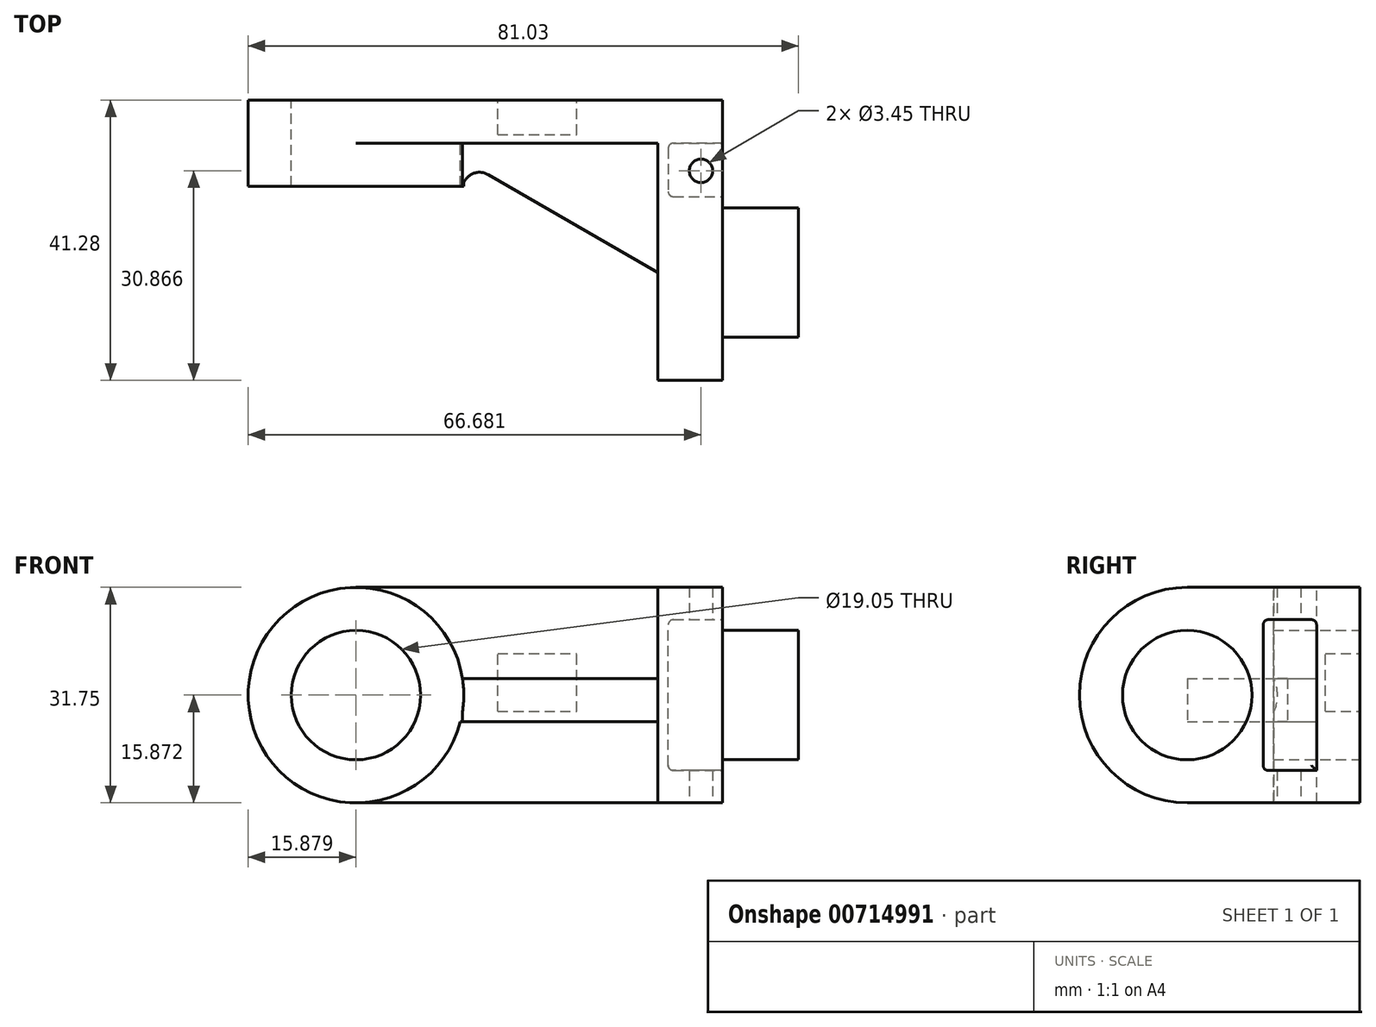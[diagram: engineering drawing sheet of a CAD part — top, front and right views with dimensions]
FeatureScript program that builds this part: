
annotation { "Feature Type Name" : "Feature", "Feature Type Description" : "" }
export const myFeature = defineFeature(function(context is Context, id is Id, definition is map)
    precondition{}
    {
        {
            var Q0;
            Q0=qCreatedBy(makeId("Front.planeOp"),FACE);
            var sketch = newSketch(context, id + "F0", { "sketchPlane" : qUnion([Q0])});
            skLineSegment(sketch, "E0", {"start": v(12.77, -13.47) * mm, "end": v(-41.2, -13.47) * mm});
            skLineSegment(sketch, "E1", {"start": v(12.77, -13.47) * mm, "end": v(12.77, 18.28) * mm});
            skLineSegment(sketch, "E2", {"start": v(12.77, 18.28) * mm, "end": v(-41.2, 18.28) * mm});
            skCircle(sketch, "E3", {"center": v(-41.2, 2.4) * mm, "radius": 15.88 * mm});
            skPoint(sketch, "E3.third.point", {"position": v(-56.86, -0.22) * mm});
            skCircle(sketch, "E4", {"center": v(-41.2, 2.4) * mm, "radius": 9.53 * mm});
            skSolve(sketch);
        }
        {
            var Q0;
            Q0 = qSketchRegion(id + "F0", true);
            extrude(context, id + "F1", {"entities" : qUnion([Q0]), "depth" : 6.35 * mm, "offsetDistance" : 25.4 * mm});
        }
        {
            var Q0;
            Q0=makeQuery(id+"F1.opExtrude","CAP_FACE",FACE,{"disambiguationData":[OSD([sQuery(id+"F0.wireOp",EDGE,"E0"),sQuery(id+"F0.wireOp",EDGE,"E1"),sQuery(id+"F0.wireOp",EDGE,"E2"),sQuery(id+"F0.wireOp",EDGE,"E3"),sQuery(id+"F0.wireOp",EDGE,"E4")])],"isStart":false});
            var sketch = newSketch(context, id + "F2", { "sketchPlane" : qUnion([Q0])});
            skCircle(sketch, "E5", {"center": v(-41.2, 2.4) * mm, "radius": 9.53 * mm});
            skCircle(sketch, "E6", {"center": v(-41.2, 2.4) * mm, "radius": 15.88 * mm});
            skSolve(sketch);
        }
        {
            var Q0;
            Q0 = qSketchRegion(id + "F2", true);
            extrude(context, id + "F3", {"entities" : qUnion([Q0]), "operationType" : NewBodyOperationType.ADD, "depth" : 6.35 * mm, "offsetDistance" : 25.4 * mm});
        }
        {
            var Q0;
            Q0=qCreatedBy(makeId("Right.planeOp"),FACE);
            cPlane(context, id + "F4", {"entities" : qUnion([Q0]), "cplaneType" : CPlaneType.OFFSET, "offset" : 12.78 * mm, "width" : 152.4 * mm, "height" : 152.4 * mm});
        }
        {
            var Q0;
            Q0=qCreatedBy(id+"F4.planeOp",FACE);
            var sketch = newSketch(context, id + "F5", { "sketchPlane" : qUnion([Q0])});
            skLineSegment(sketch, "E7", {"start": v(-6.35, -13.47) * mm, "end": v(-25.4, -13.47) * mm});
            skLineSegment(sketch, "E8", {"start": v(-6.35, 18.28) * mm, "end": v(-25.4, 18.28) * mm});
            skArc(sketch, "E9", {"start": v(-25.4, 18.28) * mm, "mid": v(-41.28, 2.4) * mm, "end": v(-25.4, -13.47) * mm});
            skLineSegment(sketch, "E10", {"start": v(-6.35, -13.47) * mm, "end": v(-6.35, 18.28) * mm});
            skSolve(sketch);
        }
        {
            var Q0;
            Q0 = qSketchRegion(id + "F5", true);
            extrude(context, id + "F6", {"entities" : qUnion([Q0]), "operationType" : NewBodyOperationType.ADD, "oppositeDirection" : true, "depth" : 9.52 * mm, "offsetDistance" : 25.4 * mm});
        }
        {
            var Q0;
            Q0=makeQuery(id+"F6.opExtrude","CAP_FACE",FACE,{"disambiguationData":[OSD([sQuery(id+"F5.wireOp",EDGE,"E7"),sQuery(id+"F5.wireOp",EDGE,"E8"),sQuery(id+"F5.wireOp",EDGE,"E9"),sQuery(id+"F5.wireOp",EDGE,"E10")])],"isStart":true});
            var sketch = newSketch(context, id + "F7", { "sketchPlane" : qUnion([Q0])});
            skCircle(sketch, "E11", {"center": v(-25.4, 2.4) * mm, "radius": 9.52 * mm});
            skSolve(sketch);
        }
        {
            var Q0;
            Q0 = qSketchRegion(id + "F7", true);
            extrude(context, id + "F8", {"entities" : qUnion([Q0]), "operationType" : NewBodyOperationType.ADD, "depth" : 11.18 * mm, "offsetDistance" : 25.4 * mm});
        }
        {
            var Q0;
            Q0=qCreatedBy(makeId("Top.planeOp"),FACE);
            var sketch = newSketch(context, id + "F9", { "sketchPlane" : qUnion([Q0])});
            skLineSegment(sketch, "E12", {"start": v(3.25, -25.4) * mm, "end": v(-21.74, -10.97) * mm});
            skLineSegment(sketch, "E13", {"start": v(3.25, -25.4) * mm, "end": v(3.25, -6.35) * mm});
            skLineSegment(sketch, "E14", {"start": v(3.25, -6.35) * mm, "end": v(-25.51, -6.35) * mm});
            skArc(sketch, "E15", {"start": v(-21.74, -10.97) * mm, "mid": v(-24.08, -10.86) * mm, "end": v(-25.51, -12.7) * mm});
            skLineSegment(sketch, "E16", {"start": v(-25.51, -12.7) * mm, "end": v(-28.97, -12.7) * mm});
            skLineSegment(sketch, "E17", {"start": v(-28.97, -6.38) * mm, "end": v(-25.51, -6.35) * mm});
            skLineSegment(sketch, "E18", {"start": v(-28.97, -6.38) * mm, "end": v(-28.97, -12.7) * mm});
            skLineSegment(sketch, "E19", {"start": v(-25.51, -12.7) * mm, "end": v(-25.51, -6.35) * mm});
            skSolve(sketch);
        }
        {
            var Q0;
            Q0 = qSketchRegion(id + "F9", true);
            extrude(context, id + "F10", {"entities" : qUnion([Q0]), "operationType" : NewBodyOperationType.ADD, "depth" : 4.83 * mm, "offsetDistance" : 25.4 * mm, "hasSecondDirection" : true, "secondDirectionOppositeDirection" : true, "secondDirectionDepth" : 1.52 * mm});
        }
        {
            var Q0;
            Q0=makeQuery(id+"F6.opExtrude","CAP_FACE",FACE,{"disambiguationData":[OSD([sQuery(id+"F5.wireOp",EDGE,"E7"),sQuery(id+"F5.wireOp",EDGE,"E8"),sQuery(id+"F5.wireOp",EDGE,"E9"),sQuery(id+"F5.wireOp",EDGE,"E10")])],"isStart":true});
            var sketch = newSketch(context, id + "F11", { "sketchPlane" : qUnion([Q0])});
            skLineSegment(sketch, "E20", {"start": v(-6.35, -8.71) * mm, "end": v(-14.22, -8.71) * mm});
            skLineSegment(sketch, "E21", {"start": v(-14.22, -8.71) * mm, "end": v(-14.22, 13.51) * mm});
            skLineSegment(sketch, "E22", {"start": v(-14.22, 13.51) * mm, "end": v(-6.35, 13.51) * mm});
            skLineSegment(sketch, "E23", {"start": v(-6.35, 13.51) * mm, "end": v(-6.35, -8.71) * mm});
            skSolve(sketch);
        }
        {
            var Q0;
            Q0 = qSketchRegion(id + "F11", true);
            extrude(context, id + "F12", {"entities" : qUnion([Q0]), "operationType" : NewBodyOperationType.REMOVE, "oppositeDirection" : true, "depth" : 8 * mm, "offsetDistance" : 25.4 * mm});
        }
        {
            var Q0;
            Q0=makeQuery(id+"F6.boolean.opBoolean","MERGE",FACE,{"derivedFrom":[makeQuery(id+"F1.opExtrude","SWEPT_FACE",FACE,{"disambiguationData":[OSD([sQuery(id+"F0.wireOp",EDGE,"E0")])]}),makeQuery(id+"F6.opExtrude","SWEPT_FACE",FACE,{"disambiguationData":[OSD([sQuery(id+"F5.wireOp",EDGE,"E7")])]})]});
            var sketch = newSketch(context, id + "F13", { "sketchPlane" : qUnion([Q0])});
            skCircle(sketch, "E24", {"center": v(9.6, 10.41) * mm, "radius": 1.73 * mm});
            skSolve(sketch);
        }
        {
            var Q0;
            Q0 = qSketchRegion(id + "F13", true);
            extrude(context, id + "F14", {"entities" : qUnion([Q0]), "operationType" : NewBodyOperationType.REMOVE, "oppositeDirection" : true, "depth" : 50.8 * mm, "offsetDistance" : 25.4 * mm});
        }
        {
            var Q0;
            Q0=makeQuery(id+"F12.boolean.opBoolean","COPY",FACE,{"derivedFrom":makeQuery(id+"F12.opExtrude","CAP_FACE",FACE,{"disambiguationData":[OSD([sQuery(id+"F11.wireOp",EDGE,"E20"),sQuery(id+"F11.wireOp",EDGE,"E21"),sQuery(id+"F11.wireOp",EDGE,"E22"),sQuery(id+"F11.wireOp",EDGE,"E23")])],"isStart":false})});
            var Q1;
            Q1=makeQuery(id+"F12.boolean.opBoolean","COPY",EDGE,{"derivedFrom":makeQuery(id+"F12.opExtrude","SWEPT_EDGE",EDGE,{"disambiguationData":[OSD([sQuery(id+"F11.wireOp",EDGE,"E21"),sQuery(id+"F11.wireOp",EDGE,"E22")])]})});
            var Q2;
            Q2=makeQuery(id+"F12.boolean.opBoolean","COPY",EDGE,{"derivedFrom":makeQuery(id+"F12.opExtrude","SWEPT_EDGE",EDGE,{"disambiguationData":[OSD([sQuery(id+"F0.wireOp",EDGE,"E1"),sQuery(id+"F5.wireOp",EDGE,"E10"),sQuery(id+"F11.wireOp",EDGE,"E22"),sQuery(id+"F11.wireOp",EDGE,"E23")])]})});
            var Q3;
            Q3=makeQuery(id+"F12.boolean.opBoolean","COPY",EDGE,{"derivedFrom":makeQuery(id+"F12.opExtrude","CAP_EDGE",EDGE,{"disambiguationData":[OSD([sQuery(id+"F11.wireOp",EDGE,"E20")])],"isStart":true})});
            var Q4;
            Q4=makeQuery(id+"F12.boolean.opBoolean","COPY",EDGE,{"derivedFrom":makeQuery(id+"F12.opExtrude","SWEPT_EDGE",EDGE,{"disambiguationData":[OSD([sQuery(id+"F11.wireOp",EDGE,"E20"),sQuery(id+"F11.wireOp",EDGE,"E21")])]})});
            fillet(context, id + "F15", {"entities" : qUnion([Q0, Q1, Q2, Q3, Q4]), "radius" : 0.76 * mm, "allowEdgeOverflow" : false});
        }
        {
            var Q0;
            Q0=makeQuery(id+"F1.opExtrude","CAP_FACE",FACE,{"disambiguationData":[OSD([sQuery(id+"F0.wireOp",EDGE,"E0"),sQuery(id+"F0.wireOp",EDGE,"E1"),sQuery(id+"F0.wireOp",EDGE,"E2"),sQuery(id+"F0.wireOp",EDGE,"E3"),sQuery(id+"F0.wireOp",EDGE,"E4")])],"isStart":true});
            var sketch = newSketch(context, id + "F16", { "sketchPlane" : qUnion([Q0])});
            skLineSegment(sketch, "E25.bottom", {"start": v(20.33, 0) * mm, "end": v(8.71, 0) * mm});
            skLineSegment(sketch, "E25.top", {"start": v(20.33, 8.56) * mm, "end": v(8.71, 8.56) * mm});
            skLineSegment(sketch, "E25.left", {"start": v(20.33, 0) * mm, "end": v(20.33, 8.56) * mm});
            skLineSegment(sketch, "E25.right", {"start": v(8.71, 0) * mm, "end": v(8.71, 8.56) * mm});
            skSolve(sketch);
        }
        {
            var Q0;
            Q0 = qSketchRegion(id + "F16", true);
            extrude(context, id + "F17", {"entities" : qUnion([Q0]), "operationType" : NewBodyOperationType.REMOVE, "oppositeDirection" : true, "depth" : 5.08 * mm, "offsetDistance" : 25.4 * mm});
        }
    });
